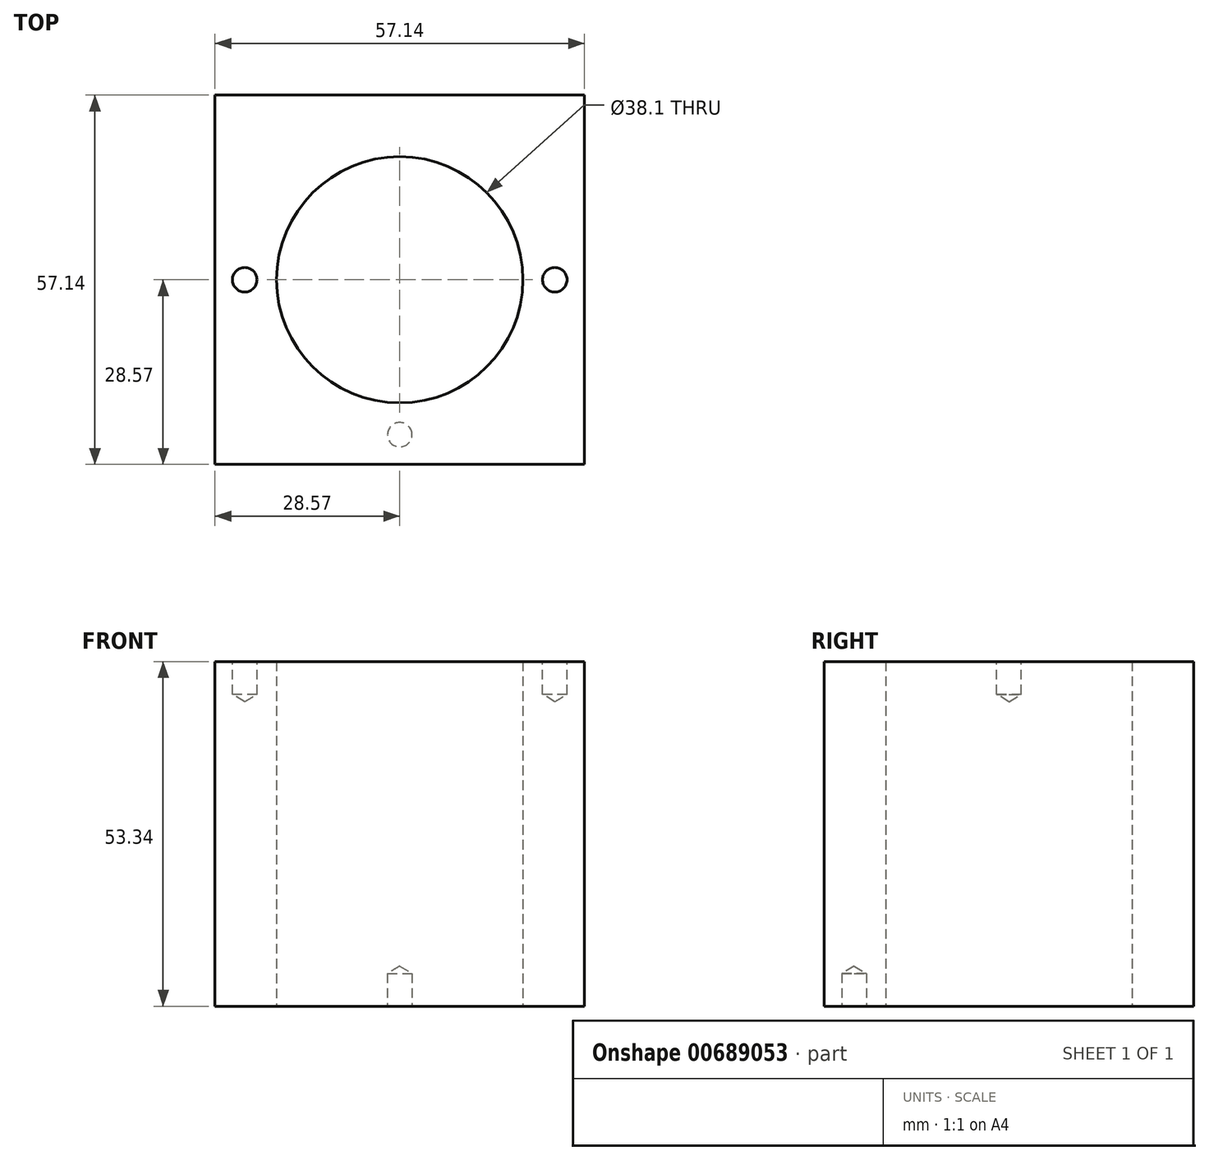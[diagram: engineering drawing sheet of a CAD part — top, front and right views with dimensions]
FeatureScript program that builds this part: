
annotation { "Feature Type Name" : "Feature", "Feature Type Description" : "" }
export const myFeature = defineFeature(function(context is Context, id is Id, definition is map)
    precondition{}
    {
        {
            var Q0;
            Q0=qCreatedBy(makeId("Top.planeOp"),FACE);
            var sketch = newSketch(context, id + "F0", { "sketchPlane" : qUnion([Q0])});
            skLineSegment(sketch, "E0.bottom", {"start": v(28.58, -28.57) * mm, "end": v(-28.57, -28.58) * mm});
            skLineSegment(sketch, "E0.top", {"start": v(28.57, 28.58) * mm, "end": v(-28.58, 28.57) * mm});
            skLineSegment(sketch, "E0.left", {"start": v(28.58, -28.57) * mm, "end": v(28.57, 28.58) * mm});
            skLineSegment(sketch, "E0.right", {"start": v(-28.58, -28.58) * mm, "end": v(-28.58, 28.57) * mm});
            skPoint(sketch, "E0.middle", {"position": v(0, 0) * mm});
            skSolve(sketch);
        }
        {
            var Q0;
            Q0=qCreatedBy(makeId("Top.planeOp"),FACE);
            var sketch = newSketch(context, id + "F1", { "sketchPlane" : qUnion([Q0])});
            skCircle(sketch, "E1", {"center": v(0, 0) * mm, "radius": 19.05 * mm});
            skSolve(sketch);
        }
        {
            var Q0;
            Q0=makeQuery(id+"F0.imprint","IMPRINT",FACE,{"disambiguationData":[TD([[makeQuery(id+"F0.imprint","IMPRINT",EDGE,{"derivedFrom":sQuery(id+"F0.wireOp",EDGE,"E0.bottom")}),-1.0]])]});
            extrude(context, id + "F2", {"entities" : qUnion([Q0]), "depth" : 53.34 * mm, "offsetDistance" : 25.4 * mm});
        }
        {
            var Q0;
            Q0=sQuery(id+"F1.wireOp",VERTEX,"E1.center");
            var Q1;
            Q1=makeQuery(id+"F2.opExtrude","SWEPT_BODY",BODY,{"disambiguationData":[OSD([sQuery(id+"F0.wireOp",EDGE,"E0.bottom"),sQuery(id+"F0.wireOp",EDGE,"E0.top"),sQuery(id+"F0.wireOp",EDGE,"E0.left"),sQuery(id+"F0.wireOp",EDGE,"E0.right")])]});
            hole(context, id + "F3", {"style" : HoleStyle.SIMPLE, "endStyle" : HoleEndStyle.THROUGH, "oppositeDirection" : true, "holeDiameter" : 38.1 * mm, "majorDiameter" : 6.35 * mm, "isTappedThrough" : true, "tappedDepth" : 3 * mm, "tapClearance" : 1, "startFromSketch" : true, "locations" : qUnion([Q0]), "scope" : qUnion([Q1])});
        }
        {
            var Q0;
            Q0=makeQuery(id+"F2.opExtrude","CAP_FACE",FACE,{"disambiguationData":[OSD([sQuery(id+"F0.wireOp",EDGE,"E0.bottom"),sQuery(id+"F0.wireOp",EDGE,"E0.top"),sQuery(id+"F0.wireOp",EDGE,"E0.left"),sQuery(id+"F0.wireOp",EDGE,"E0.right")])],"isStart":true});
            var sketch = newSketch(context, id + "F4", { "sketchPlane" : qUnion([Q0])});
            skCircle(sketch, "E2", {"center": v(0, 0) * mm, "radius": 21.59 * mm, "construction": true});
            skSolve(sketch);
        }
        {
            var Q0;
            Q0=makeQuery(id+"F4.imprint","IMPRINT",FACE,{"disambiguationData":[TD([[makeQuery(id+"F4.imprint","IMPRINT",EDGE,{"derivedFrom":makeQuery(id+"F2.opExtrude","CAP_EDGE",EDGE,{"disambiguationData":[OSD([sQuery(id+"F0.wireOp",EDGE,"E0.bottom")])],"isStart":true})}),1.0]])]});
            var sketch = newSketch(context, id + "F5", { "sketchPlane" : qUnion([Q0])});
            skCircle(sketch, "E3", {"center": v(0, 0) * mm, "radius": 23.97 * mm, "construction": true});
            skPoint(sketch, "E4", {"position": v(0, 23.97) * mm});
            skSolve(sketch);
        }
        {
            var Q0;
            Q0=sQuery(id+"F5.wireOp",VERTEX,"E4");
            var Q1;
            Q1=makeQuery(id+"F2.opExtrude","SWEPT_BODY",BODY,{"disambiguationData":[OSD([sQuery(id+"F0.wireOp",EDGE,"E0.bottom"),sQuery(id+"F0.wireOp",EDGE,"E0.top"),sQuery(id+"F0.wireOp",EDGE,"E0.left"),sQuery(id+"F0.wireOp",EDGE,"E0.right")])]});
            hole(context, id + "F6", {"style" : HoleStyle.SIMPLE, "endStyle" : HoleEndStyle.BLIND, "standardTappedOrClearance" : lookupTablePath({ "standard" : "ANSI", "engagement" : "75%", "pitch" : "24 tpi", "size" : "#10", "type" : "Tapped" }), "standardBlindInLast" : lookupTablePath({ "standard" : "ANSI", "engagement" : "75%", "pitch" : "24 tpi", "size" : "#10", "type" : "Tapped" }), "holeDiameter" : 3.8 * mm, "majorDiameter" : 4.83 * mm, "showTappedDepth" : true, "holeDepth" : 5.08 * mm, "isTappedThrough" : true, "tappedDepth" : 4.02 * mm, "tapClearance" : 1, "startFromSketch" : true, "locations" : qUnion([Q0]), "scope" : qUnion([Q1])});
        }
        {
            var Q0;
            Q0=makeQuery(id+"F2.opExtrude","CAP_FACE",FACE,{"disambiguationData":[OSD([sQuery(id+"F0.wireOp",EDGE,"E0.bottom"),sQuery(id+"F0.wireOp",EDGE,"E0.top"),sQuery(id+"F0.wireOp",EDGE,"E0.left"),sQuery(id+"F0.wireOp",EDGE,"E0.right")])],"isStart":false});
            var sketch = newSketch(context, id + "F7", { "sketchPlane" : qUnion([Q0])});
            skCircle(sketch, "E5", {"center": v(0, 0) * mm, "radius": 23.98 * mm, "construction": true});
            skPoint(sketch, "E6", {"position": v(-23.98, 0) * mm});
            skPoint(sketch, "E7", {"position": v(23.98, 0) * mm});
            skSolve(sketch);
        }
        {
            var Q0;
            Q0=sQuery(id+"F7.wireOp",VERTEX,"E6");
            var Q1;
            Q1=sQuery(id+"F7.wireOp",VERTEX,"E7");
            var Q2;
            Q2=makeQuery(id+"F2.opExtrude","SWEPT_BODY",BODY,{"disambiguationData":[OSD([sQuery(id+"F0.wireOp",EDGE,"E0.bottom"),sQuery(id+"F0.wireOp",EDGE,"E0.top"),sQuery(id+"F0.wireOp",EDGE,"E0.left"),sQuery(id+"F0.wireOp",EDGE,"E0.right")])]});
            hole(context, id + "F8", {"style" : HoleStyle.SIMPLE, "endStyle" : HoleEndStyle.BLIND, "standardTappedOrClearance" : lookupTablePath({ "standard" : "ANSI", "engagement" : "75%", "pitch" : "24 tpi", "size" : "#10", "type" : "Tapped" }), "standardBlindInLast" : lookupTablePath({ "standard" : "ANSI", "engagement" : "75%", "pitch" : "24 tpi", "size" : "#10", "type" : "Tapped" }), "holeDiameter" : 3.8 * mm, "majorDiameter" : 4.83 * mm, "showTappedDepth" : true, "holeDepth" : 5.08 * mm, "isTappedThrough" : true, "tappedDepth" : 4.02 * mm, "tapClearance" : 1, "startFromSketch" : true, "locations" : qUnion([Q0, Q1]), "scope" : qUnion([Q2])});
        }
    });
